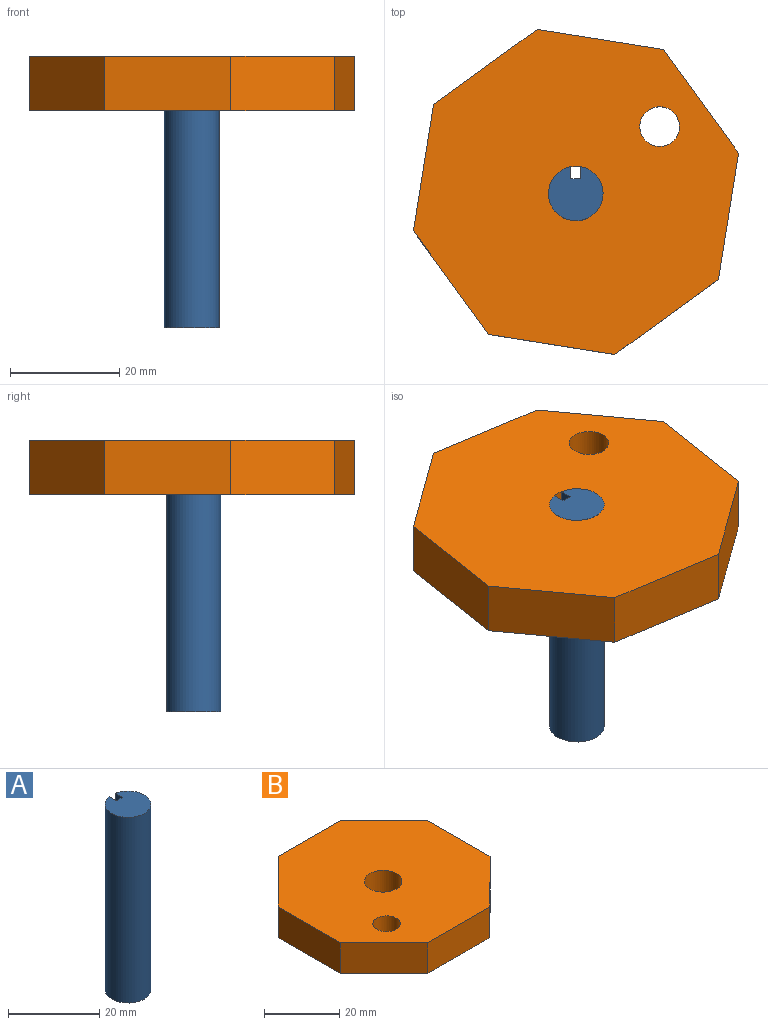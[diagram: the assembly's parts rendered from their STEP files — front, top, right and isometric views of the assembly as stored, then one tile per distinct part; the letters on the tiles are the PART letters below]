
ASSEMBLY  parts=2 mates=1
PART A: 6 faces, bbox 10x9.9x49.7 mm
  f0: cylinder r=5mm len=49.7mm, axis (0,0,1), area 1470mm2, adj f1,f2,f3,f5
  f1: plane 10x9.92mm, normal (0,0,-1), area 74.4mm2, adj f0,f3,f4,f5
  f2: plane 10x9.92mm, normal (0,0,1), area 74.4mm2, adj f0,f3,f4,f5
  f3: plane 49.7x2.23mm, normal (1,0,0), area 110.6mm2, adj f0,f1,f2,f4
  f4: plane 49.7x1.83mm, normal (0,1,0), area 90.8mm2, adj f1,f2,f3,f5
  f5: plane 49.7x2.23mm, normal (-1,0,0), area 110.6mm2, adj f0,f1,f2,f4
PART B: 12 faces, bbox 56.5x56.5x10 mm
  f0: plane 16.56x16.56mm, normal (0.71,0.71,0), area 234.1mm2, adj f1,f7,f8,f9
  f1: plane 23.41x10mm, normal (0,1,0), area 234.1mm2, adj f0,f2,f8,f9
  f2: plane 16.56x16.56mm, normal (-0.71,0.71,0), area 234.1mm2, adj f1,f3,f8,f9
  f3: plane 23.41x10mm, normal (-1,0,0), area 234.1mm2, adj f2,f4,f8,f9
  f4: plane 16.56x16.56mm, normal (-0.71,-0.71,0), area 234.1mm2, adj f3,f5,f8,f9
  f5: plane 23.41x10mm, normal (0,-1,0), area 234.1mm2, adj f4,f6,f8,f9
  f6: plane 16.56x16.56mm, normal (0.71,-0.71,0), area 234.1mm2, adj f5,f7,f8,f9
  f7: plane 23.41x10mm, normal (1,0,0), area 234.1mm2, adj f0,f6,f8,f9
  f8: plane 56.53x56.53mm, normal (0,0,1), area 2526.7mm2, adj f0,f1,f2,f3,f4,f5,f6,f7
  f9: plane 56.53x56.53mm, normal (0,0,-1), area 2526.7mm2, adj f0,f1,f2,f3,f4,f5,f6,f7
  f10: cylinder r=3.64mm len=10mm, axis (0,0,1), area 228.7mm2, adj f8,f9
  f11: cylinder r=5mm len=10mm, axis (0,0,1), area 314.2mm2, adj f8,f9
PLACE A t=(2.68,-8.21,-28.17)mm fixed
PLACE B rot(axis=(0,0,1),171deg) t=(7.16,48.53,-3.17)mm
MATE revolute B.f11 <-> A.f0  axis (0,0,1) through (2.68,20.34,6.83)mm
